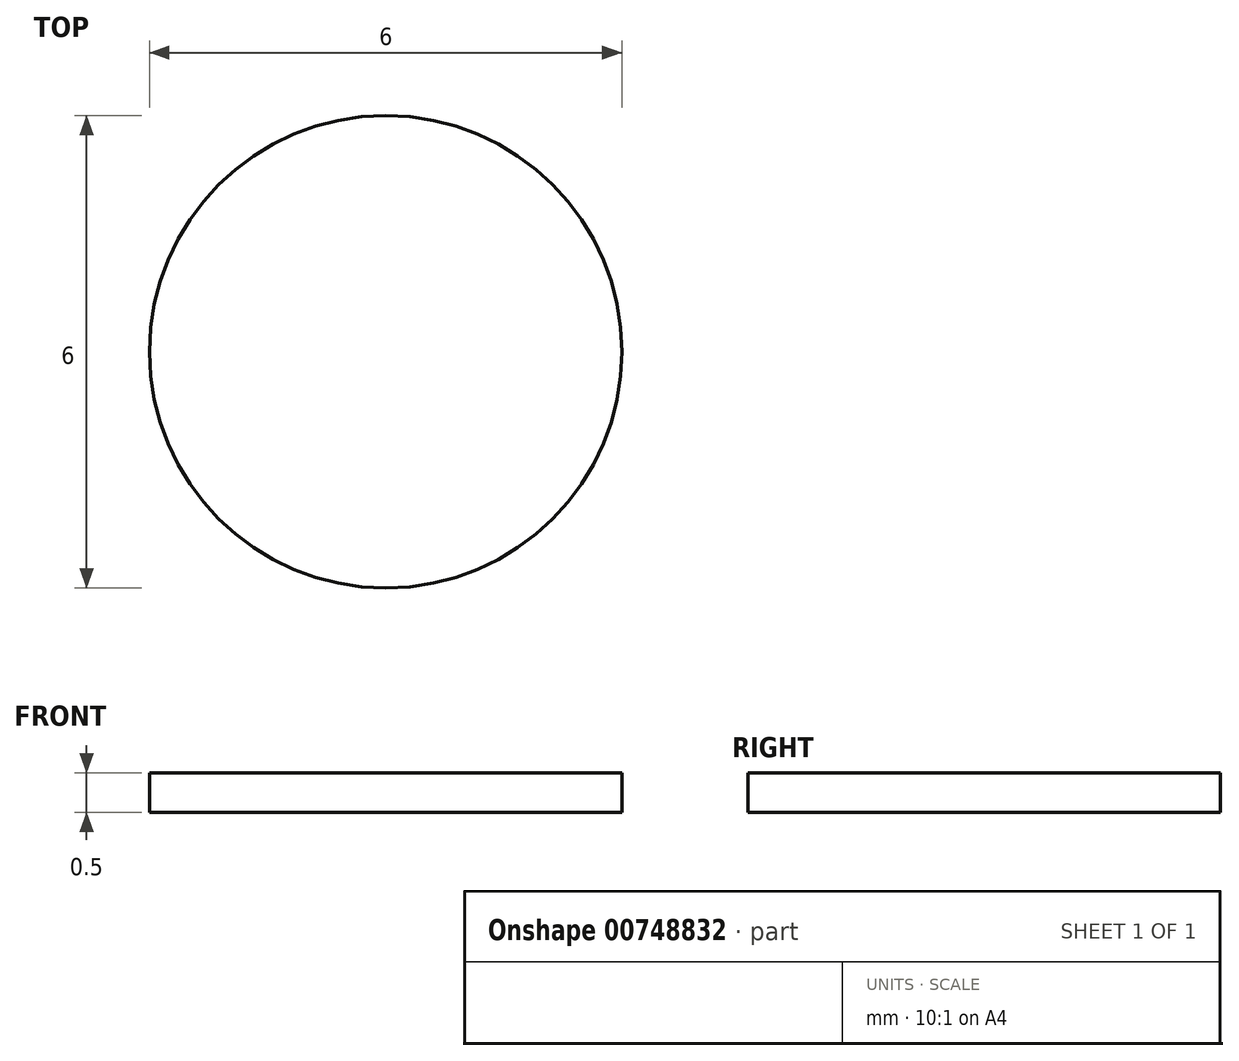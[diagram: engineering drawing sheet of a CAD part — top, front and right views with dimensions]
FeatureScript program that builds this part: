
annotation { "Feature Type Name" : "Feature", "Feature Type Description" : "" }
export const myFeature = defineFeature(function(context is Context, id is Id, definition is map)
    precondition{}
    {
        {
            var Q0;
            Q0=qCreatedBy(makeId("Top.planeOp"),FACE);
            var sketch = newSketch(context, id + "F0", { "sketchPlane" : qUnion([Q0])});
            skCircle(sketch, "E0", {"center": v(0, 0) * mm, "radius": 3 * mm});
            skSolve(sketch);
        }
        {
            var Q0;
            Q0 = qSketchRegion(id + "F0", true);
            extrude(context, id + "F1", {"entities" : qUnion([Q0]), "depth" : 0.5 * mm, "offsetDistance" : 25 * mm});
        }
    });
